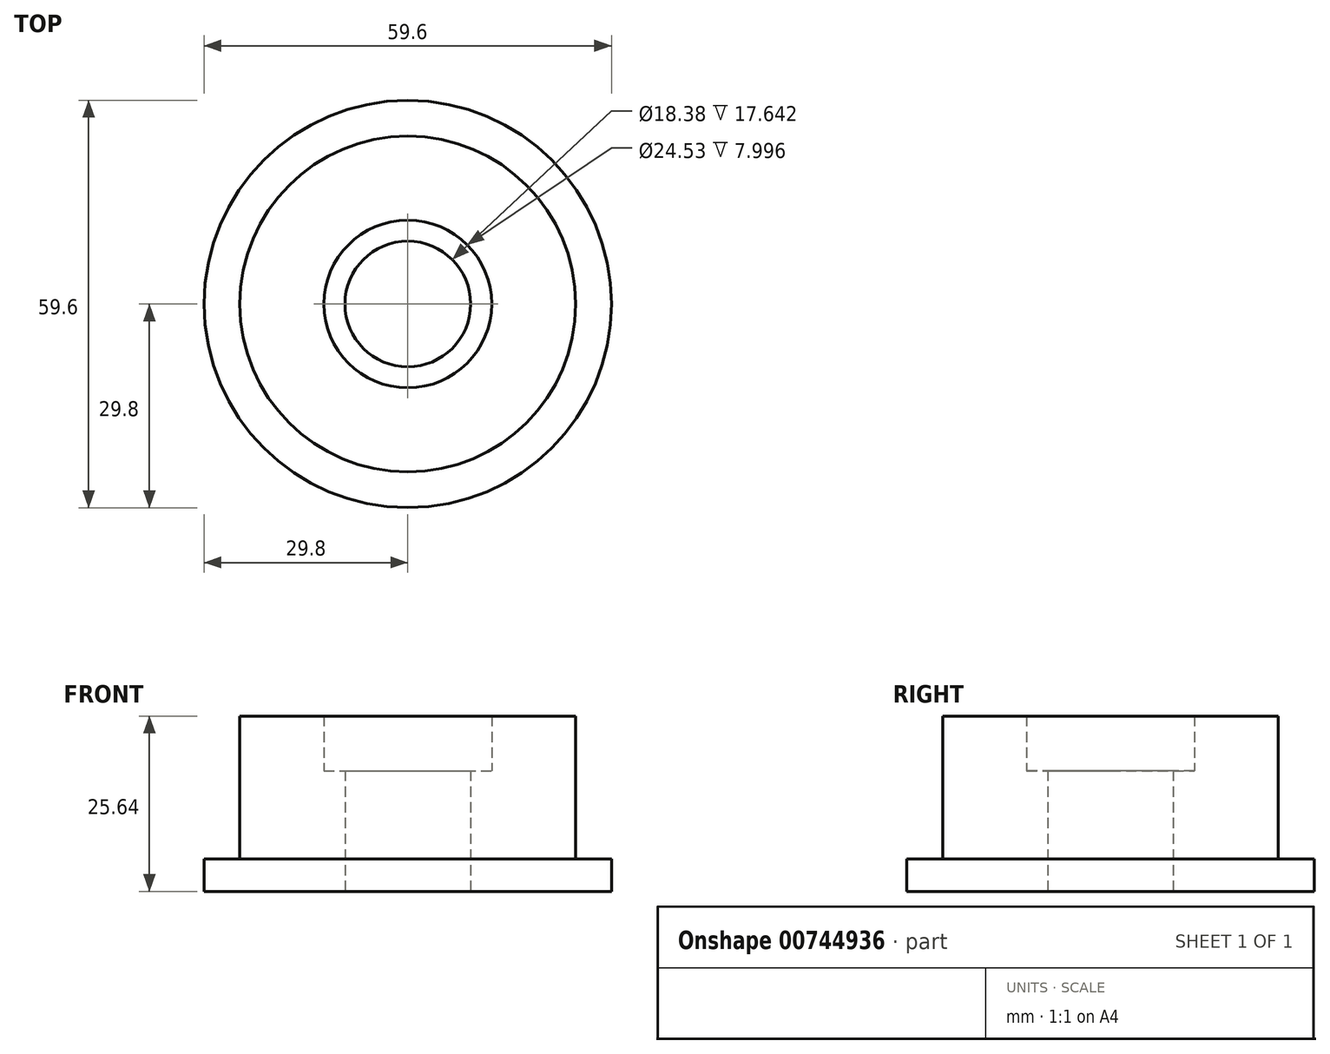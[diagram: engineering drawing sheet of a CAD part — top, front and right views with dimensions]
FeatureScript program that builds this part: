
annotation { "Feature Type Name" : "Feature", "Feature Type Description" : "" }
export const myFeature = defineFeature(function(context is Context, id is Id, definition is map)
    precondition{}
    {
        {
            var Q0;
            Q0=qCreatedBy(makeId("Front.planeOp"),FACE);
            var sketch = newSketch(context, id + "F0", { "sketchPlane" : qUnion([Q0])});
            skLineSegment(sketch, "E0", {"start": v(9.2, 0) * mm, "end": v(29.8, 0) * mm});
            skLineSegment(sketch, "E1", {"start": v(29.8, 0) * mm, "end": v(29.8, 4.73) * mm});
            skLineSegment(sketch, "E2", {"start": v(29.8, 4.73) * mm, "end": v(24.57, 4.73) * mm});
            skLineSegment(sketch, "E3", {"start": v(24.57, 4.73) * mm, "end": v(24.57, 25.64) * mm});
            skLineSegment(sketch, "E4", {"start": v(24.57, 25.64) * mm, "end": v(12.27, 25.64) * mm});
            skLineSegment(sketch, "E5", {"start": v(12.27, 25.64) * mm, "end": v(12.27, 17.64) * mm});
            skLineSegment(sketch, "E6", {"start": v(12.27, 17.64) * mm, "end": v(9.2, 17.64) * mm});
            skLineSegment(sketch, "E7", {"start": v(9.2, 17.64) * mm, "end": v(9.2, 0) * mm});
            skLineSegment(sketch, "E8", {"start": v(0, 0) * mm, "end": v(0, 55.46) * mm, "construction": true});
            skSolve(sketch);
        }
        {
            var Q0;
            Q0=makeQuery(id+"F0.imprint","IMPRINT",FACE,{"disambiguationData":[TD([[makeQuery(id+"F0.imprint","IMPRINT",EDGE,{"derivedFrom":sQuery(id+"F0.wireOp",EDGE,"E0")}),1.0]])]});
            var Q1;
            Q1=sQuery(id+"F0.wireOp",EDGE,"E8");
            revolve(context, id + "F1", {"surfaceOperationType" : NewSurfaceOperationType.NEW, "entities" : qUnion([Q0]), "axis" : qUnion([Q1]), "revolveType" : RevolveType.FULL});
        }
    });
